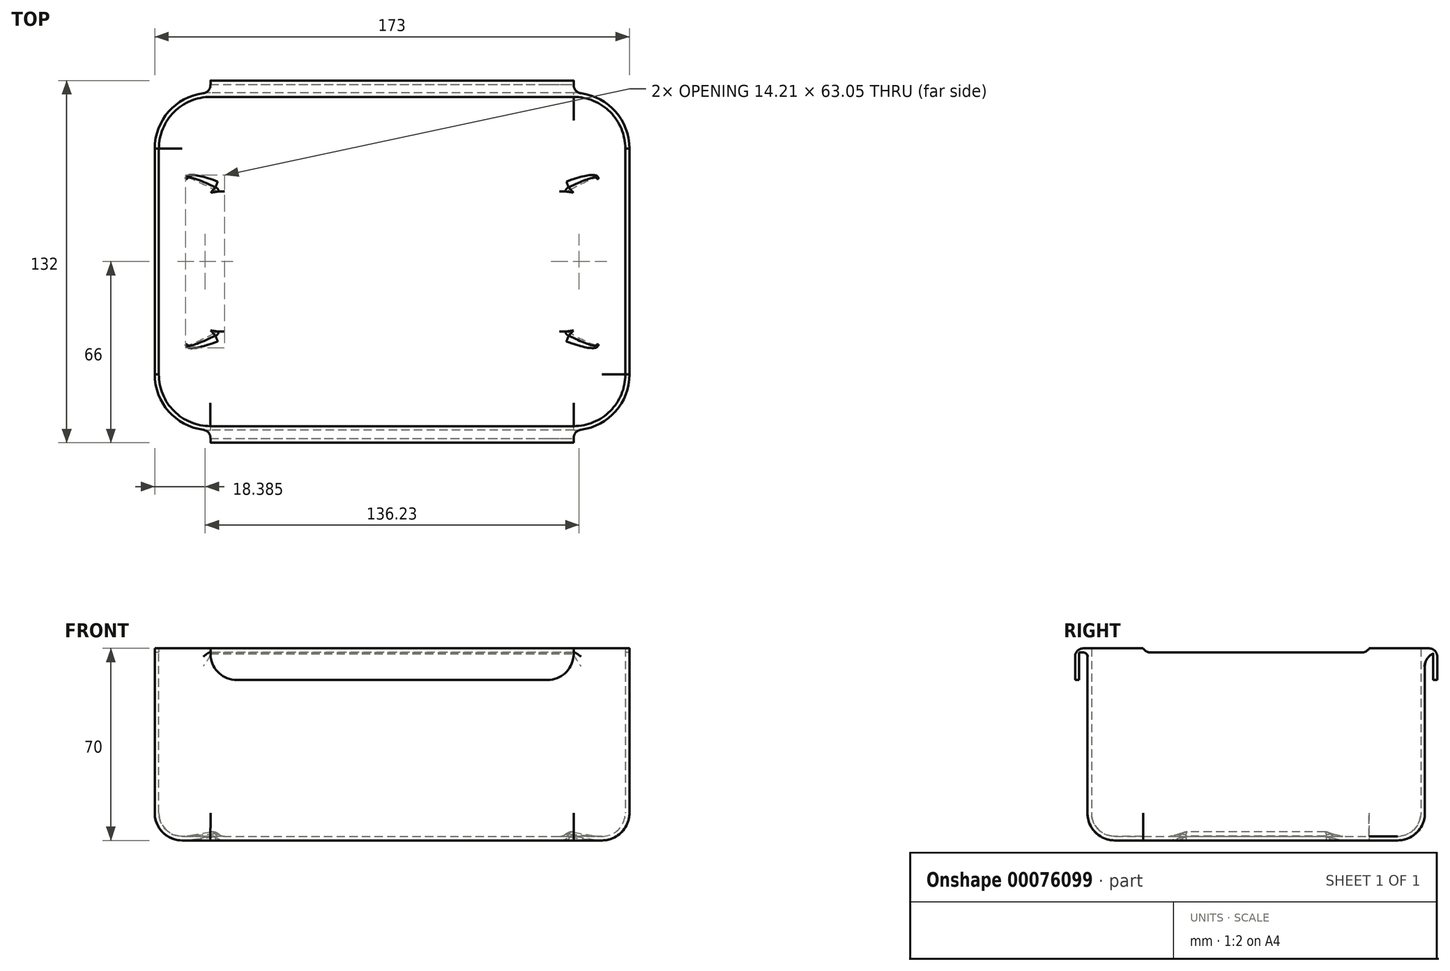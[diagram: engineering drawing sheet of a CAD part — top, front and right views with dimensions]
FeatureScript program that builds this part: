
annotation { "Feature Type Name" : "Feature", "Feature Type Description" : "" }
export const myFeature = defineFeature(function(context is Context, id is Id, definition is map)
    precondition{}
    {
        {
            var Q0;
            Q0=qCreatedBy(makeId("Top.planeOp"),FACE);
            var sketch = newSketch(context, id + "F0", { "sketchPlane" : qUnion([Q0])});
            skLineSegment(sketch, "E0.bottom", {"start": v(66.18, -61.5) * mm, "end": v(-66.18, -61.5) * mm});
            skLineSegment(sketch, "E0.top", {"start": v(66.18, 61.5) * mm, "end": v(-66.18, 61.5) * mm});
            skLineSegment(sketch, "E0.left", {"start": v(86.5, -41.18) * mm, "end": v(86.5, 41.18) * mm});
            skLineSegment(sketch, "E0.right", {"start": v(-86.5, -41.18) * mm, "end": v(-86.5, 41.18) * mm});
            skPoint(sketch, "E0.middle", {"position": v(0, 0) * mm});
            skPoint(sketch, "E1.visualSharp", {"position": v(-86.5, 61.5) * mm});
            skArc(sketch, "E1.filletArc", {"start": v(-66.18, 61.5) * mm, "mid": v(-80.55, 55.55) * mm, "end": v(-86.5, 41.18) * mm});
            skPoint(sketch, "E2.visualSharp", {"position": v(86.5, 61.5) * mm});
            skArc(sketch, "E2.filletArc", {"start": v(86.5, 41.18) * mm, "mid": v(80.55, 55.55) * mm, "end": v(66.18, 61.5) * mm});
            skPoint(sketch, "E3.visualSharp", {"position": v(86.5, -61.5) * mm});
            skArc(sketch, "E3.filletArc", {"start": v(66.18, -61.5) * mm, "mid": v(80.55, -55.55) * mm, "end": v(86.5, -41.18) * mm});
            skPoint(sketch, "E4.visualSharp", {"position": v(-86.5, -61.5) * mm});
            skArc(sketch, "E4.filletArc", {"start": v(-86.5, -41.18) * mm, "mid": v(-80.55, -55.55) * mm, "end": v(-66.18, -61.5) * mm});
            skSolve(sketch);
        }
        {
            var Q0;
            Q0=makeQuery(id+"F0.imprint","IMPRINT",FACE,{"disambiguationData":[TD([[makeQuery(id+"F0.imprint","IMPRINT",EDGE,{"derivedFrom":sQuery(id+"F0.wireOp",EDGE,"E0.bottom")}),-1.0]])]});
            extrude(context, id + "F1", {"entities" : qUnion([Q0]), "depth" : 70 * mm});
        }
        {
            var Q0;
            Q0=makeQuery(id+"F1.opExtrude","CAP_FACE",FACE,{"disambiguationData":[OSD([sQuery(id+"F0.wireOp",EDGE,"E0.bottom"),sQuery(id+"F0.wireOp",EDGE,"E0.top"),sQuery(id+"F0.wireOp",EDGE,"E0.left"),sQuery(id+"F0.wireOp",EDGE,"E0.right"),sQuery(id+"F0.wireOp",EDGE,"E1.filletArc"),sQuery(id+"F0.wireOp",EDGE,"E2.filletArc"),sQuery(id+"F0.wireOp",EDGE,"E3.filletArc"),sQuery(id+"F0.wireOp",EDGE,"E4.filletArc")])],"isStart":true});
            fillet(context, id + "F2", {"entities" : qUnion([Q0]), "radius" : 10 * mm, "tangentPropagation" : true, "allowEdgeOverflow" : false});
        }
        {
            var Q0;
            Q0=makeQuery(id+"F1.opExtrude","CAP_FACE",FACE,{"disambiguationData":[OSD([sQuery(id+"F0.wireOp",EDGE,"E0.bottom"),sQuery(id+"F0.wireOp",EDGE,"E0.top"),sQuery(id+"F0.wireOp",EDGE,"E0.left"),sQuery(id+"F0.wireOp",EDGE,"E0.right"),sQuery(id+"F0.wireOp",EDGE,"E1.filletArc"),sQuery(id+"F0.wireOp",EDGE,"E2.filletArc"),sQuery(id+"F0.wireOp",EDGE,"E3.filletArc"),sQuery(id+"F0.wireOp",EDGE,"E4.filletArc")])],"isStart":true});
            var sketch = newSketch(context, id + "F3", { "sketchPlane" : qUnion([Q0])});
            skLineSegment(sketch, "E5", {"start": v(74.78, 0) * mm, "end": v(74.78, 32.96) * mm});
            skLineSegment(sketch, "E6", {"start": v(74.78, 32.96) * mm, "end": v(62.04, 25.39) * mm});
            skLineSegment(sketch, "E7", {"start": v(62.04, 25.39) * mm, "end": v(62.04, 0) * mm});
            skLineSegment(sketch, "E8.MirrorCS", {"start": v(62.04, -25.39) * mm, "end": v(62.04, 0) * mm});
            skLineSegment(sketch, "E9.MirrorCS", {"start": v(74.78, 0) * mm, "end": v(74.78, -32.96) * mm});
            skLineSegment(sketch, "E10.MirrorCS", {"start": v(74.78, -32.96) * mm, "end": v(62.04, -25.39) * mm});
            skLineSegment(sketch, "E11.MirrorCS", {"start": v(-74.78, 0) * mm, "end": v(-74.78, -32.96) * mm});
            skLineSegment(sketch, "E12.MirrorCS", {"start": v(-74.78, -32.96) * mm, "end": v(-62.04, -25.39) * mm});
            skLineSegment(sketch, "E13.MirrorCS", {"start": v(-62.04, -25.39) * mm, "end": v(-62.04, 0) * mm});
            skLineSegment(sketch, "E14.MirrorCS", {"start": v(-62.04, 25.39) * mm, "end": v(-62.04, 0) * mm});
            skLineSegment(sketch, "E15.MirrorCS", {"start": v(-74.78, 0) * mm, "end": v(-74.78, 32.96) * mm});
            skLineSegment(sketch, "E16.MirrorCS", {"start": v(-74.78, 32.96) * mm, "end": v(-62.04, 25.39) * mm});
            skSolve(sketch);
        }
        {
            var Q0;
            Q0 = qSketchRegion(id + "F3", true);
            extrude(context, id + "F4", {"entities" : qUnion([Q0]), "operationType" : NewBodyOperationType.REMOVE, "oppositeDirection" : true, "depth" : 2 * mm});
        }
        {
            var Q0;
            Q0=makeQuery(id+"F4.boolean.opBoolean","COPY",EDGE,{"derivedFrom":makeQuery(id+"F4.opExtrude","CAP_EDGE",EDGE,{"disambiguationData":[OSD([sQuery(id+"F3.wireOp",EDGE,"E11.MirrorCS"),sQuery(id+"F3.wireOp",EDGE,"E15.MirrorCS")])],"isStart":false})});
            var Q1;
            Q1=makeQuery(id+"F4.boolean.opBoolean","COPY",EDGE,{"derivedFrom":makeQuery(id+"F4.opExtrude","CAP_EDGE",EDGE,{"disambiguationData":[OSD([sQuery(id+"F3.wireOp",EDGE,"E5"),sQuery(id+"F3.wireOp",EDGE,"E9.MirrorCS")])],"isStart":false})});
            chamfer(context, id + "F5", {"entities" : qUnion([Q0, Q1]), "chamferType" : ChamferType.OFFSET_ANGLE, "width" : 2 * mm, "oppositeDirection" : false, "angle" : 80 * degree, "tangentPropagation" : true});
        }
        {
            var Q0;
            Q0=makeQuery(id+"F4.boolean.opBoolean","COPY",EDGE,{"derivedFrom":makeQuery(id+"F4.opExtrude","CAP_EDGE",EDGE,{"disambiguationData":[OSD([sQuery(id+"F3.wireOp",EDGE,"E13.MirrorCS"),sQuery(id+"F3.wireOp",EDGE,"E14.MirrorCS")])],"isStart":false})});
            var Q1;
            Q1=makeQuery(id+"F4.boolean.opBoolean","COPY",EDGE,{"derivedFrom":makeQuery(id+"F4.opExtrude","CAP_EDGE",EDGE,{"disambiguationData":[OSD([sQuery(id+"F3.wireOp",EDGE,"E7"),sQuery(id+"F3.wireOp",EDGE,"E8.MirrorCS")])],"isStart":false})});
            chamfer(context, id + "F6", {"entities" : qUnion([Q0, Q1]), "width" : 3 * mm, "tangentPropagation" : true});
        }
        {
            var Q0;
            Q0=makeQuery(id+"F5.opChamfer","BLEND_EDGE",EDGE,{"blendedFrom":[makeQuery(id+"F4.boolean.opBoolean","COPY",EDGE,{"derivedFrom":makeQuery(id+"F4.opExtrude","CAP_EDGE",EDGE,{"disambiguationData":[OSD([sQuery(id+"F3.wireOp",EDGE,"E5"),sQuery(id+"F3.wireOp",EDGE,"E9.MirrorCS")])],"isStart":false})}),makeQuery(id+"F4.boolean.opBoolean","COPY",FACE,{"derivedFrom":makeQuery(id+"F4.opExtrude","SWEPT_FACE",FACE,{"disambiguationData":[OSD([sQuery(id+"F3.wireOp",EDGE,"E10.MirrorCS")])]})})],"blendedInto":[makeQuery(id+"F4.boolean.opBoolean","COPY",FACE,{"derivedFrom":makeQuery(id+"F4.opExtrude","SWEPT_FACE",FACE,{"disambiguationData":[OSD([sQuery(id+"F3.wireOp",EDGE,"E10.MirrorCS")])]})})]});
            var Q1;
            Q1=makeQuery(id+"F6.opChamfer","BLEND_EDGE",EDGE,{"blendedFrom":[makeQuery(id+"F4.boolean.opBoolean","COPY",EDGE,{"derivedFrom":makeQuery(id+"F4.opExtrude","CAP_EDGE",EDGE,{"disambiguationData":[OSD([sQuery(id+"F3.wireOp",EDGE,"E7"),sQuery(id+"F3.wireOp",EDGE,"E8.MirrorCS")])],"isStart":false})}),makeQuery(id+"F5.opChamfer","BLEND_FACE",FACE,{"disambiguationData":[OSD([sQuery(id+"F3.wireOp",EDGE,"E5"),sQuery(id+"F3.wireOp",EDGE,"E9.MirrorCS")])]})],"blendedInto":[makeQuery(id+"F5.opChamfer","BLEND_FACE",FACE,{"disambiguationData":[OSD([sQuery(id+"F3.wireOp",EDGE,"E5"),sQuery(id+"F3.wireOp",EDGE,"E9.MirrorCS")])]})]});
            var Q2;
            Q2=makeQuery(id+"F5.opChamfer","BLEND_EDGE",EDGE,{"blendedFrom":[makeQuery(id+"F4.boolean.opBoolean","COPY",EDGE,{"derivedFrom":makeQuery(id+"F4.opExtrude","CAP_EDGE",EDGE,{"disambiguationData":[OSD([sQuery(id+"F3.wireOp",EDGE,"E5"),sQuery(id+"F3.wireOp",EDGE,"E9.MirrorCS")])],"isStart":false})}),makeQuery(id+"F4.boolean.opBoolean","COPY",FACE,{"derivedFrom":makeQuery(id+"F4.opExtrude","SWEPT_FACE",FACE,{"disambiguationData":[OSD([sQuery(id+"F3.wireOp",EDGE,"E6")])]})})],"blendedInto":[makeQuery(id+"F4.boolean.opBoolean","COPY",FACE,{"derivedFrom":makeQuery(id+"F4.opExtrude","SWEPT_FACE",FACE,{"disambiguationData":[OSD([sQuery(id+"F3.wireOp",EDGE,"E6")])]})})]});
            var Q3;
            Q3=makeQuery(id+"F6.opChamfer","BLEND_EDGE",EDGE,{"blendedFrom":[makeQuery(id+"F4.boolean.opBoolean","COPY",EDGE,{"derivedFrom":makeQuery(id+"F4.opExtrude","CAP_EDGE",EDGE,{"disambiguationData":[OSD([sQuery(id+"F3.wireOp",EDGE,"E13.MirrorCS"),sQuery(id+"F3.wireOp",EDGE,"E14.MirrorCS")])],"isStart":false})}),makeQuery(id+"F5.opChamfer","BLEND_FACE",FACE,{"disambiguationData":[OSD([sQuery(id+"F3.wireOp",EDGE,"E11.MirrorCS"),sQuery(id+"F3.wireOp",EDGE,"E15.MirrorCS")])]})],"blendedInto":[makeQuery(id+"F5.opChamfer","BLEND_FACE",FACE,{"disambiguationData":[OSD([sQuery(id+"F3.wireOp",EDGE,"E11.MirrorCS"),sQuery(id+"F3.wireOp",EDGE,"E15.MirrorCS")])]})]});
            var Q4;
            Q4=makeQuery(id+"F5.opChamfer","BLEND_EDGE",EDGE,{"blendedFrom":[makeQuery(id+"F4.boolean.opBoolean","COPY",EDGE,{"derivedFrom":makeQuery(id+"F4.opExtrude","CAP_EDGE",EDGE,{"disambiguationData":[OSD([sQuery(id+"F3.wireOp",EDGE,"E11.MirrorCS"),sQuery(id+"F3.wireOp",EDGE,"E15.MirrorCS")])],"isStart":false})}),makeQuery(id+"F4.boolean.opBoolean","COPY",FACE,{"derivedFrom":makeQuery(id+"F4.opExtrude","SWEPT_FACE",FACE,{"disambiguationData":[OSD([sQuery(id+"F3.wireOp",EDGE,"E16.MirrorCS")])]})})],"blendedInto":[makeQuery(id+"F4.boolean.opBoolean","COPY",FACE,{"derivedFrom":makeQuery(id+"F4.opExtrude","SWEPT_FACE",FACE,{"disambiguationData":[OSD([sQuery(id+"F3.wireOp",EDGE,"E16.MirrorCS")])]})})]});
            var Q5;
            Q5=makeQuery(id+"F5.opChamfer","BLEND_EDGE",EDGE,{"blendedFrom":[makeQuery(id+"F4.boolean.opBoolean","COPY",EDGE,{"derivedFrom":makeQuery(id+"F4.opExtrude","CAP_EDGE",EDGE,{"disambiguationData":[OSD([sQuery(id+"F3.wireOp",EDGE,"E11.MirrorCS"),sQuery(id+"F3.wireOp",EDGE,"E15.MirrorCS")])],"isStart":false})}),makeQuery(id+"F4.boolean.opBoolean","COPY",FACE,{"derivedFrom":makeQuery(id+"F4.opExtrude","SWEPT_FACE",FACE,{"disambiguationData":[OSD([sQuery(id+"F3.wireOp",EDGE,"E12.MirrorCS")])]})})],"blendedInto":[makeQuery(id+"F4.boolean.opBoolean","COPY",FACE,{"derivedFrom":makeQuery(id+"F4.opExtrude","SWEPT_FACE",FACE,{"disambiguationData":[OSD([sQuery(id+"F3.wireOp",EDGE,"E12.MirrorCS")])]})})]});
            fillet(context, id + "F7", {"entities" : qUnion([Q0, Q1, Q2, Q3, Q4, Q5]), "radius" : 2 * mm, "tangentPropagation" : true, "allowEdgeOverflow" : false});
        }
        {
            var Q0;
            {var subQ0=sQuery(id+"F3.wireOp",EDGE,"E15.MirrorCS");var subQ1=sQuery(id+"F3.wireOp",EDGE,"E11.MirrorCS");Q0=makeQuery(id+"F7.opFillet","BLEND_EDGE",EDGE,{"blendedFrom":[makeQuery(id+"F6.opChamfer","BLEND_EDGE",EDGE,{"blendedFrom":[makeQuery(id+"F4.boolean.opBoolean","COPY",EDGE,{"derivedFrom":makeQuery(id+"F4.opExtrude","CAP_EDGE",EDGE,{"disambiguationData":[OSD([sQuery(id+"F3.wireOp",EDGE,"E13.MirrorCS"),sQuery(id+"F3.wireOp",EDGE,"E14.MirrorCS")])],"isStart":false})}),makeQuery(id+"F5.opChamfer","BLEND_FACE",FACE,{"disambiguationData":[OSD([subQ1,subQ0])]})],"blendedInto":[makeQuery(id+"F5.opChamfer","BLEND_FACE",FACE,{"disambiguationData":[OSD([subQ1,subQ0])]})]}),makeQuery(id+"F5.opChamfer","BLEND_EDGE",EDGE,{"blendedFrom":[makeQuery(id+"F4.boolean.opBoolean","COPY",EDGE,{"derivedFrom":makeQuery(id+"F4.opExtrude","CAP_EDGE",EDGE,{"disambiguationData":[OSD([subQ1,subQ0])],"isStart":false})}),makeQuery(id+"F4.boolean.opBoolean","COPY",FACE,{"derivedFrom":makeQuery(id+"F4.opExtrude","SWEPT_FACE",FACE,{"disambiguationData":[OSD([sQuery(id+"F3.wireOp",EDGE,"E16.MirrorCS")])]})})],"blendedInto":[makeQuery(id+"F4.boolean.opBoolean","COPY",FACE,{"derivedFrom":makeQuery(id+"F4.opExtrude","SWEPT_FACE",FACE,{"disambiguationData":[OSD([sQuery(id+"F3.wireOp",EDGE,"E16.MirrorCS")])]})})]})],"blendedInto":[]});}
            var Q1;
            Q1=makeQuery(id+"F7.opFillet","BLEND_EDGE",EDGE,{"blendedFrom":[makeQuery(id+"F5.opChamfer","BLEND_EDGE",EDGE,{"blendedFrom":[makeQuery(id+"F4.boolean.opBoolean","COPY",EDGE,{"derivedFrom":makeQuery(id+"F4.opExtrude","CAP_EDGE",EDGE,{"disambiguationData":[OSD([sQuery(id+"F3.wireOp",EDGE,"E11.MirrorCS"),sQuery(id+"F3.wireOp",EDGE,"E15.MirrorCS")])],"isStart":false})}),makeQuery(id+"F4.boolean.opBoolean","COPY",FACE,{"derivedFrom":makeQuery(id+"F4.opExtrude","SWEPT_FACE",FACE,{"disambiguationData":[OSD([sQuery(id+"F3.wireOp",EDGE,"E16.MirrorCS")])]})})],"blendedInto":[makeQuery(id+"F4.boolean.opBoolean","COPY",FACE,{"derivedFrom":makeQuery(id+"F4.opExtrude","SWEPT_FACE",FACE,{"disambiguationData":[OSD([sQuery(id+"F3.wireOp",EDGE,"E16.MirrorCS")])]})})]}),makeQuery(id+"F6.opChamfer","BLEND_FACE",FACE,{"disambiguationData":[OSD([sQuery(id+"F3.wireOp",EDGE,"E13.MirrorCS"),sQuery(id+"F3.wireOp",EDGE,"E14.MirrorCS")])]})],"blendedInto":[makeQuery(id+"F6.opChamfer","BLEND_FACE",FACE,{"disambiguationData":[OSD([sQuery(id+"F3.wireOp",EDGE,"E13.MirrorCS"),sQuery(id+"F3.wireOp",EDGE,"E14.MirrorCS")])]})]});
            var Q2;
            {var subQ0=sQuery(id+"F3.wireOp",EDGE,"E15.MirrorCS");var subQ1=sQuery(id+"F3.wireOp",EDGE,"E11.MirrorCS");Q2=makeQuery(id+"F7.opFillet","BLEND_EDGE",EDGE,{"blendedFrom":[makeQuery(id+"F6.opChamfer","BLEND_EDGE",EDGE,{"blendedFrom":[makeQuery(id+"F4.boolean.opBoolean","COPY",EDGE,{"derivedFrom":makeQuery(id+"F4.opExtrude","CAP_EDGE",EDGE,{"disambiguationData":[OSD([sQuery(id+"F3.wireOp",EDGE,"E13.MirrorCS"),sQuery(id+"F3.wireOp",EDGE,"E14.MirrorCS")])],"isStart":false})}),makeQuery(id+"F5.opChamfer","BLEND_FACE",FACE,{"disambiguationData":[OSD([subQ1,subQ0])]})],"blendedInto":[makeQuery(id+"F5.opChamfer","BLEND_FACE",FACE,{"disambiguationData":[OSD([subQ1,subQ0])]})]}),makeQuery(id+"F5.opChamfer","BLEND_EDGE",EDGE,{"blendedFrom":[makeQuery(id+"F4.boolean.opBoolean","COPY",EDGE,{"derivedFrom":makeQuery(id+"F4.opExtrude","CAP_EDGE",EDGE,{"disambiguationData":[OSD([subQ1,subQ0])],"isStart":false})}),makeQuery(id+"F4.boolean.opBoolean","COPY",FACE,{"derivedFrom":makeQuery(id+"F4.opExtrude","SWEPT_FACE",FACE,{"disambiguationData":[OSD([sQuery(id+"F3.wireOp",EDGE,"E12.MirrorCS")])]})})],"blendedInto":[makeQuery(id+"F4.boolean.opBoolean","COPY",FACE,{"derivedFrom":makeQuery(id+"F4.opExtrude","SWEPT_FACE",FACE,{"disambiguationData":[OSD([sQuery(id+"F3.wireOp",EDGE,"E12.MirrorCS")])]})})]})],"blendedInto":[]});}
            var Q3;
            {var subQ0=sQuery(id+"F3.wireOp",EDGE,"E9.MirrorCS");var subQ1=sQuery(id+"F3.wireOp",EDGE,"E5");Q3=makeQuery(id+"F7.opFillet","BLEND_EDGE",EDGE,{"blendedFrom":[makeQuery(id+"F6.opChamfer","BLEND_EDGE",EDGE,{"blendedFrom":[makeQuery(id+"F4.boolean.opBoolean","COPY",EDGE,{"derivedFrom":makeQuery(id+"F4.opExtrude","CAP_EDGE",EDGE,{"disambiguationData":[OSD([sQuery(id+"F3.wireOp",EDGE,"E7"),sQuery(id+"F3.wireOp",EDGE,"E8.MirrorCS")])],"isStart":false})}),makeQuery(id+"F5.opChamfer","BLEND_FACE",FACE,{"disambiguationData":[OSD([subQ1,subQ0])]})],"blendedInto":[makeQuery(id+"F5.opChamfer","BLEND_FACE",FACE,{"disambiguationData":[OSD([subQ1,subQ0])]})]}),makeQuery(id+"F5.opChamfer","BLEND_EDGE",EDGE,{"blendedFrom":[makeQuery(id+"F4.boolean.opBoolean","COPY",EDGE,{"derivedFrom":makeQuery(id+"F4.opExtrude","CAP_EDGE",EDGE,{"disambiguationData":[OSD([subQ1,subQ0])],"isStart":false})}),makeQuery(id+"F4.boolean.opBoolean","COPY",FACE,{"derivedFrom":makeQuery(id+"F4.opExtrude","SWEPT_FACE",FACE,{"disambiguationData":[OSD([sQuery(id+"F3.wireOp",EDGE,"E6")])]})})],"blendedInto":[makeQuery(id+"F4.boolean.opBoolean","COPY",FACE,{"derivedFrom":makeQuery(id+"F4.opExtrude","SWEPT_FACE",FACE,{"disambiguationData":[OSD([sQuery(id+"F3.wireOp",EDGE,"E6")])]})})]})],"blendedInto":[]});}
            var Q4;
            {var subQ0=sQuery(id+"F3.wireOp",EDGE,"E9.MirrorCS");var subQ1=sQuery(id+"F3.wireOp",EDGE,"E5");Q4=makeQuery(id+"F7.opFillet","BLEND_EDGE",EDGE,{"blendedFrom":[makeQuery(id+"F6.opChamfer","BLEND_EDGE",EDGE,{"blendedFrom":[makeQuery(id+"F4.boolean.opBoolean","COPY",EDGE,{"derivedFrom":makeQuery(id+"F4.opExtrude","CAP_EDGE",EDGE,{"disambiguationData":[OSD([sQuery(id+"F3.wireOp",EDGE,"E7"),sQuery(id+"F3.wireOp",EDGE,"E8.MirrorCS")])],"isStart":false})}),makeQuery(id+"F5.opChamfer","BLEND_FACE",FACE,{"disambiguationData":[OSD([subQ1,subQ0])]})],"blendedInto":[makeQuery(id+"F5.opChamfer","BLEND_FACE",FACE,{"disambiguationData":[OSD([subQ1,subQ0])]})]}),makeQuery(id+"F5.opChamfer","BLEND_EDGE",EDGE,{"blendedFrom":[makeQuery(id+"F4.boolean.opBoolean","COPY",EDGE,{"derivedFrom":makeQuery(id+"F4.opExtrude","CAP_EDGE",EDGE,{"disambiguationData":[OSD([subQ1,subQ0])],"isStart":false})}),makeQuery(id+"F4.boolean.opBoolean","COPY",FACE,{"derivedFrom":makeQuery(id+"F4.opExtrude","SWEPT_FACE",FACE,{"disambiguationData":[OSD([sQuery(id+"F3.wireOp",EDGE,"E10.MirrorCS")])]})})],"blendedInto":[makeQuery(id+"F4.boolean.opBoolean","COPY",FACE,{"derivedFrom":makeQuery(id+"F4.opExtrude","SWEPT_FACE",FACE,{"disambiguationData":[OSD([sQuery(id+"F3.wireOp",EDGE,"E10.MirrorCS")])]})})]})],"blendedInto":[]});}
            fillet(context, id + "F8", {"entities" : qUnion([Q0, Q1, Q2, Q3, Q4]), "radius" : 1 * mm, "tangentPropagation" : true, "allowEdgeOverflow" : false});
        }
        {
            var Q0;
            Q0=makeQuery(id+"F6.opChamfer","BLEND_EDGE",EDGE,{"blendedFrom":[makeQuery(id+"F4.boolean.opBoolean","COPY",EDGE,{"derivedFrom":makeQuery(id+"F4.opExtrude","CAP_EDGE",EDGE,{"disambiguationData":[OSD([sQuery(id+"F3.wireOp",EDGE,"E7"),sQuery(id+"F3.wireOp",EDGE,"E8.MirrorCS")])],"isStart":false})}),makeQuery(id+"F1.opExtrude","CAP_FACE",FACE,{"disambiguationData":[OSD([sQuery(id+"F0.wireOp",EDGE,"E0.bottom"),sQuery(id+"F0.wireOp",EDGE,"E0.top"),sQuery(id+"F0.wireOp",EDGE,"E0.left"),sQuery(id+"F0.wireOp",EDGE,"E0.right"),sQuery(id+"F0.wireOp",EDGE,"E1.filletArc"),sQuery(id+"F0.wireOp",EDGE,"E2.filletArc"),sQuery(id+"F0.wireOp",EDGE,"E3.filletArc"),sQuery(id+"F0.wireOp",EDGE,"E4.filletArc")])],"isStart":true})],"blendedInto":[makeQuery(id+"F1.opExtrude","CAP_FACE",FACE,{"disambiguationData":[OSD([sQuery(id+"F0.wireOp",EDGE,"E0.bottom"),sQuery(id+"F0.wireOp",EDGE,"E0.top"),sQuery(id+"F0.wireOp",EDGE,"E0.left"),sQuery(id+"F0.wireOp",EDGE,"E0.right"),sQuery(id+"F0.wireOp",EDGE,"E1.filletArc"),sQuery(id+"F0.wireOp",EDGE,"E2.filletArc"),sQuery(id+"F0.wireOp",EDGE,"E3.filletArc"),sQuery(id+"F0.wireOp",EDGE,"E4.filletArc")])],"isStart":true})]});
            var Q1;
            Q1=makeQuery(id+"F6.opChamfer","BLEND_EDGE",EDGE,{"blendedFrom":[makeQuery(id+"F4.boolean.opBoolean","COPY",EDGE,{"derivedFrom":makeQuery(id+"F4.opExtrude","CAP_EDGE",EDGE,{"disambiguationData":[OSD([sQuery(id+"F3.wireOp",EDGE,"E13.MirrorCS"),sQuery(id+"F3.wireOp",EDGE,"E14.MirrorCS")])],"isStart":false})}),makeQuery(id+"F1.opExtrude","CAP_FACE",FACE,{"disambiguationData":[OSD([sQuery(id+"F0.wireOp",EDGE,"E0.bottom"),sQuery(id+"F0.wireOp",EDGE,"E0.top"),sQuery(id+"F0.wireOp",EDGE,"E0.left"),sQuery(id+"F0.wireOp",EDGE,"E0.right"),sQuery(id+"F0.wireOp",EDGE,"E1.filletArc"),sQuery(id+"F0.wireOp",EDGE,"E2.filletArc"),sQuery(id+"F0.wireOp",EDGE,"E3.filletArc"),sQuery(id+"F0.wireOp",EDGE,"E4.filletArc")])],"isStart":true})],"blendedInto":[makeQuery(id+"F1.opExtrude","CAP_FACE",FACE,{"disambiguationData":[OSD([sQuery(id+"F0.wireOp",EDGE,"E0.bottom"),sQuery(id+"F0.wireOp",EDGE,"E0.top"),sQuery(id+"F0.wireOp",EDGE,"E0.left"),sQuery(id+"F0.wireOp",EDGE,"E0.right"),sQuery(id+"F0.wireOp",EDGE,"E1.filletArc"),sQuery(id+"F0.wireOp",EDGE,"E2.filletArc"),sQuery(id+"F0.wireOp",EDGE,"E3.filletArc"),sQuery(id+"F0.wireOp",EDGE,"E4.filletArc")])],"isStart":true})]});
            fillet(context, id + "F9", {"entities" : qUnion([Q0, Q1]), "radius" : 5 * mm, "tangentPropagation" : true, "allowEdgeOverflow" : false});
        }
        {
            var Q0;
            Q0=makeQuery(id+"F1.opExtrude","CAP_FACE",FACE,{"disambiguationData":[OSD([sQuery(id+"F0.wireOp",EDGE,"E0.bottom"),sQuery(id+"F0.wireOp",EDGE,"E0.top"),sQuery(id+"F0.wireOp",EDGE,"E0.left"),sQuery(id+"F0.wireOp",EDGE,"E0.right"),sQuery(id+"F0.wireOp",EDGE,"E1.filletArc"),sQuery(id+"F0.wireOp",EDGE,"E2.filletArc"),sQuery(id+"F0.wireOp",EDGE,"E3.filletArc"),sQuery(id+"F0.wireOp",EDGE,"E4.filletArc")])],"isStart":false});
            var sketch = newSketch(context, id + "F10", { "sketchPlane" : qUnion([Q0])});
            skLineSegment(sketch, "E17.top", {"start": v(-66.18, 66) * mm, "end": v(66.18, 66) * mm});
            skLineSegment(sketch, "E17.left", {"start": v(-66.18, 61.5) * mm, "end": v(-66.18, 66) * mm});
            skLineSegment(sketch, "E17.right", {"start": v(66.18, 61.5) * mm, "end": v(66.18, 66) * mm});
            skLineSegment(sketch, "E18.top", {"start": v(-66.18, -66) * mm, "end": v(66.18, -66) * mm});
            skLineSegment(sketch, "E18.left", {"start": v(-66.18, -61.5) * mm, "end": v(-66.18, -66) * mm});
            skLineSegment(sketch, "E18.right", {"start": v(66.18, -61.5) * mm, "end": v(66.18, -66) * mm});
            skArc(sketch, "E19.0", {"start": v(-66.18, 61.5) * mm, "mid": v(-80.55, 55.55) * mm, "end": v(-86.5, 41.18) * mm});
            skLineSegment(sketch, "E19.1", {"start": v(-86.5, -41.18) * mm, "end": v(-86.5, 41.18) * mm});
            skArc(sketch, "E19.2", {"start": v(-86.5, -41.18) * mm, "mid": v(-80.55, -55.55) * mm, "end": v(-66.18, -61.5) * mm});
            skArc(sketch, "E19.3", {"start": v(66.18, -61.5) * mm, "mid": v(80.55, -55.55) * mm, "end": v(86.5, -41.18) * mm});
            skLineSegment(sketch, "E19.4", {"start": v(86.5, -41.18) * mm, "end": v(86.5, 41.18) * mm});
            skArc(sketch, "E19.5", {"start": v(86.5, 41.18) * mm, "mid": v(80.55, 55.55) * mm, "end": v(66.18, 61.5) * mm});
            skSolve(sketch);
        }
        {
            var Q0;
            Q0 = qSketchRegion(id + "F10", true);
            extrude(context, id + "F11", {"entities" : qUnion([Q0]), "operationType" : NewBodyOperationType.ADD, "oppositeDirection" : true, "depth" : 1.5 * mm});
        }
        {
            var Q0;
            Q0=makeQuery(id+"F11.boolean.opBoolean","MERGE",FACE,{"derivedFrom":[makeQuery(id+"F1.opExtrude","CAP_FACE",FACE,{"disambiguationData":[OSD([sQuery(id+"F0.wireOp",EDGE,"E0.bottom"),sQuery(id+"F0.wireOp",EDGE,"E0.top"),sQuery(id+"F0.wireOp",EDGE,"E0.left"),sQuery(id+"F0.wireOp",EDGE,"E0.right"),sQuery(id+"F0.wireOp",EDGE,"E1.filletArc"),sQuery(id+"F0.wireOp",EDGE,"E2.filletArc"),sQuery(id+"F0.wireOp",EDGE,"E3.filletArc"),sQuery(id+"F0.wireOp",EDGE,"E4.filletArc")])],"isStart":false}),makeQuery(id+"F11.opExtrude","CAP_FACE",FACE,{"disambiguationData":[OSD([sQuery(id+"F10.wireOp",EDGE,"E17.top"),sQuery(id+"F10.wireOp",EDGE,"E17.left"),sQuery(id+"F10.wireOp",EDGE,"E17.right"),sQuery(id+"F10.wireOp",EDGE,"E18.top"),sQuery(id+"F10.wireOp",EDGE,"E18.left"),sQuery(id+"F10.wireOp",EDGE,"E18.right"),sQuery(id+"F10.wireOp",EDGE,"E19.0"),sQuery(id+"F10.wireOp",EDGE,"E19.1"),sQuery(id+"F10.wireOp",EDGE,"E19.2"),sQuery(id+"F10.wireOp",EDGE,"E19.3"),sQuery(id+"F10.wireOp",EDGE,"E19.4"),sQuery(id+"F10.wireOp",EDGE,"E19.5")])],"isStart":true})]});
            shell(context, id + "F12", {"entities" : qUnion([Q0]), "thickness" : 1.5 * mm});
        }
        {
            var Q0;
            {var subQ0=sQuery(id+"F10.wireOp",EDGE,"E17.top");var subQ1=sQuery(id+"F10.wireOp",EDGE,"E17.left");var subQ2=sQuery(id+"F10.wireOp",EDGE,"E17.right");Q0=makeQuery(id+"F11.boolean.opBoolean","SPLIT",FACE,{"disambiguationData":[TD([makeQuery(id+"F1.opExtrude","SWEPT_FACE",FACE,{"disambiguationData":[OSD([sQuery(id+"F0.wireOp",EDGE,"E0.top")])]})])],"derivedFrom":makeQuery(id+"F11.opExtrude","CAP_FACE",FACE,{"disambiguationData":[OSD([subQ0,subQ1,subQ2,sQuery(id+"F10.wireOp",EDGE,"E18.top"),sQuery(id+"F10.wireOp",EDGE,"E18.left"),sQuery(id+"F10.wireOp",EDGE,"E18.right"),sQuery(id+"F10.wireOp",EDGE,"E19.0"),sQuery(id+"F10.wireOp",EDGE,"E19.1"),sQuery(id+"F10.wireOp",EDGE,"E19.2"),sQuery(id+"F10.wireOp",EDGE,"E19.3"),sQuery(id+"F10.wireOp",EDGE,"E19.4"),sQuery(id+"F10.wireOp",EDGE,"E19.5")])],"isStart":false})});}
            var sketch = newSketch(context, id + "F13", { "sketchPlane" : qUnion([Q0])});
            skLineSegment(sketch, "E20.bottom", {"start": v(-66.18, -66) * mm, "end": v(66.18, -66) * mm});
            skLineSegment(sketch, "E20.top", {"start": v(-66.18, -64.5) * mm, "end": v(66.18, -64.5) * mm});
            skLineSegment(sketch, "E20.left", {"start": v(-66.18, -66) * mm, "end": v(-66.18, -64.5) * mm});
            skLineSegment(sketch, "E20.right", {"start": v(66.18, -66) * mm, "end": v(66.18, -64.5) * mm});
            skSolve(sketch);
        }
        {
            var Q0;
            Q0 = qSketchRegion(id + "F13", true);
            extrude(context, id + "F14", {"entities" : qUnion([Q0]), "operationType" : NewBodyOperationType.ADD, "depth" : 10 * mm});
        }
        {
            var Q0;
            {var subQ0=sQuery(id+"F10.wireOp",EDGE,"E18.top");var subQ1=sQuery(id+"F10.wireOp",EDGE,"E18.left");var subQ2=sQuery(id+"F10.wireOp",EDGE,"E18.right");Q0=makeQuery(id+"F11.boolean.opBoolean","SPLIT",FACE,{"disambiguationData":[TD([makeQuery(id+"F1.opExtrude","SWEPT_FACE",FACE,{"disambiguationData":[OSD([sQuery(id+"F0.wireOp",EDGE,"E0.bottom")])]})])],"derivedFrom":makeQuery(id+"F11.opExtrude","CAP_FACE",FACE,{"disambiguationData":[OSD([sQuery(id+"F10.wireOp",EDGE,"E17.top"),sQuery(id+"F10.wireOp",EDGE,"E17.left"),sQuery(id+"F10.wireOp",EDGE,"E17.right"),subQ0,subQ1,subQ2,sQuery(id+"F10.wireOp",EDGE,"E19.0"),sQuery(id+"F10.wireOp",EDGE,"E19.1"),sQuery(id+"F10.wireOp",EDGE,"E19.2"),sQuery(id+"F10.wireOp",EDGE,"E19.3"),sQuery(id+"F10.wireOp",EDGE,"E19.4"),sQuery(id+"F10.wireOp",EDGE,"E19.5")])],"isStart":false})});}
            var sketch = newSketch(context, id + "F15", { "sketchPlane" : qUnion([Q0])});
            skLineSegment(sketch, "E21.bottom", {"start": v(-66.18, 66) * mm, "end": v(66.18, 66) * mm});
            skLineSegment(sketch, "E21.top", {"start": v(-66.18, 64.5) * mm, "end": v(66.18, 64.5) * mm});
            skLineSegment(sketch, "E21.left", {"start": v(-66.18, 66) * mm, "end": v(-66.18, 64.5) * mm});
            skLineSegment(sketch, "E21.right", {"start": v(66.18, 66) * mm, "end": v(66.18, 64.5) * mm});
            skSolve(sketch);
        }
        {
            var Q0;
            Q0 = qSketchRegion(id + "F15", true);
            extrude(context, id + "F16", {"entities" : qUnion([Q0]), "operationType" : NewBodyOperationType.ADD, "depth" : 10 * mm});
        }
        {
            var Q0;
            {var subQ0=sQuery(id+"F0.wireOp",EDGE,"E0.bottom");Q0=makeQuery(id+"F11.boolean.opBoolean","MERGE",EDGE,{"derivedFrom":[makeQuery(id+"F1.opExtrude","SWEPT_EDGE",EDGE,{"disambiguationData":[OSD([subQ0,sQuery(id+"F0.wireOp",EDGE,"E4.filletArc")])]}),makeQuery(id+"F11.opExtrude","SWEPT_EDGE",EDGE,{"disambiguationData":[OSD([subQ0,sQuery(id+"F10.wireOp",EDGE,"E18.left"),sQuery(id+"F10.wireOp",EDGE,"E19.2")])]})]});}
            var Q1;
            {var subQ0=sQuery(id+"F0.wireOp",EDGE,"E0.bottom");Q1=makeQuery(id+"F11.boolean.opBoolean","MERGE",EDGE,{"derivedFrom":[makeQuery(id+"F1.opExtrude","SWEPT_EDGE",EDGE,{"disambiguationData":[OSD([subQ0,sQuery(id+"F0.wireOp",EDGE,"E3.filletArc")])]}),makeQuery(id+"F11.opExtrude","SWEPT_EDGE",EDGE,{"disambiguationData":[OSD([subQ0,sQuery(id+"F10.wireOp",EDGE,"E18.right"),sQuery(id+"F10.wireOp",EDGE,"E19.3")])]})]});}
            var Q2;
            {var subQ0=sQuery(id+"F0.wireOp",EDGE,"E0.top");Q2=makeQuery(id+"F11.boolean.opBoolean","MERGE",EDGE,{"derivedFrom":[makeQuery(id+"F1.opExtrude","SWEPT_EDGE",EDGE,{"disambiguationData":[OSD([subQ0,sQuery(id+"F0.wireOp",EDGE,"E2.filletArc")])]}),makeQuery(id+"F11.opExtrude","SWEPT_EDGE",EDGE,{"disambiguationData":[OSD([subQ0,sQuery(id+"F10.wireOp",EDGE,"E17.right"),sQuery(id+"F10.wireOp",EDGE,"E19.5")])]})]});}
            var Q3;
            {var subQ0=sQuery(id+"F0.wireOp",EDGE,"E0.top");Q3=makeQuery(id+"F11.boolean.opBoolean","MERGE",EDGE,{"derivedFrom":[makeQuery(id+"F1.opExtrude","SWEPT_EDGE",EDGE,{"disambiguationData":[OSD([subQ0,sQuery(id+"F0.wireOp",EDGE,"E1.filletArc")])]}),makeQuery(id+"F11.opExtrude","SWEPT_EDGE",EDGE,{"disambiguationData":[OSD([subQ0,sQuery(id+"F10.wireOp",EDGE,"E17.left"),sQuery(id+"F10.wireOp",EDGE,"E19.0")])]})]});}
            fillet(context, id + "F17", {"entities" : qUnion([Q0, Q1, Q2, Q3]), "radius" : 3.03 * mm, "tangentPropagation" : true, "allowEdgeOverflow" : false});
        }
        {
            var Q0;
            Q0=makeQuery(id+"F11.boolean.opBoolean","INTERSECT",EDGE,{"derivedFrom":[makeQuery(id+"F1.opExtrude","SWEPT_FACE",FACE,{"disambiguationData":[OSD([sQuery(id+"F0.wireOp",EDGE,"E0.top")])]}),makeQuery(id+"F11.opExtrude","CAP_FACE",FACE,{"disambiguationData":[OSD([sQuery(id+"F10.wireOp",EDGE,"E17.top"),sQuery(id+"F10.wireOp",EDGE,"E17.left"),sQuery(id+"F10.wireOp",EDGE,"E17.right"),sQuery(id+"F10.wireOp",EDGE,"E18.top"),sQuery(id+"F10.wireOp",EDGE,"E18.left"),sQuery(id+"F10.wireOp",EDGE,"E18.right"),sQuery(id+"F10.wireOp",EDGE,"E19.0"),sQuery(id+"F10.wireOp",EDGE,"E19.1"),sQuery(id+"F10.wireOp",EDGE,"E19.2"),sQuery(id+"F10.wireOp",EDGE,"E19.3"),sQuery(id+"F10.wireOp",EDGE,"E19.4"),sQuery(id+"F10.wireOp",EDGE,"E19.5")])],"isStart":false})]});
            fillet(context, id + "F18", {"entities" : qUnion([Q0]), "radius" : 5 * mm, "tangentPropagation" : true, "allowEdgeOverflow" : false});
        }
        {
            var Q0;
            Q0=makeQuery(id+"F11.boolean.opBoolean","INTERSECT",EDGE,{"derivedFrom":[makeQuery(id+"F1.opExtrude","SWEPT_FACE",FACE,{"disambiguationData":[OSD([sQuery(id+"F0.wireOp",EDGE,"E0.top")])]}),makeQuery(id+"F11.opExtrude","CAP_FACE",FACE,{"disambiguationData":[OSD([sQuery(id+"F10.wireOp",EDGE,"E17.top"),sQuery(id+"F10.wireOp",EDGE,"E17.left"),sQuery(id+"F10.wireOp",EDGE,"E17.right"),sQuery(id+"F10.wireOp",EDGE,"E18.top"),sQuery(id+"F10.wireOp",EDGE,"E18.left"),sQuery(id+"F10.wireOp",EDGE,"E18.right"),sQuery(id+"F10.wireOp",EDGE,"E19.0"),sQuery(id+"F10.wireOp",EDGE,"E19.1"),sQuery(id+"F10.wireOp",EDGE,"E19.2"),sQuery(id+"F10.wireOp",EDGE,"E19.3"),sQuery(id+"F10.wireOp",EDGE,"E19.4"),sQuery(id+"F10.wireOp",EDGE,"E19.5")])],"isStart":false})]});
            var Q1;
            Q1=makeQuery(id+"F14.opExtrude","CAP_EDGE",EDGE,{"disambiguationData":[OSD([sQuery(id+"F13.wireOp",EDGE,"E20.top")])],"isStart":true});
            var Q2;
            Q2=makeQuery(id+"F11.boolean.opBoolean","INTERSECT",EDGE,{"derivedFrom":[makeQuery(id+"F1.opExtrude","SWEPT_FACE",FACE,{"disambiguationData":[OSD([sQuery(id+"F0.wireOp",EDGE,"E0.bottom")])]}),makeQuery(id+"F11.opExtrude","CAP_FACE",FACE,{"disambiguationData":[OSD([sQuery(id+"F10.wireOp",EDGE,"E17.top"),sQuery(id+"F10.wireOp",EDGE,"E17.left"),sQuery(id+"F10.wireOp",EDGE,"E17.right"),sQuery(id+"F10.wireOp",EDGE,"E18.top"),sQuery(id+"F10.wireOp",EDGE,"E18.left"),sQuery(id+"F10.wireOp",EDGE,"E18.right"),sQuery(id+"F10.wireOp",EDGE,"E19.0"),sQuery(id+"F10.wireOp",EDGE,"E19.1"),sQuery(id+"F10.wireOp",EDGE,"E19.2"),sQuery(id+"F10.wireOp",EDGE,"E19.3"),sQuery(id+"F10.wireOp",EDGE,"E19.4"),sQuery(id+"F10.wireOp",EDGE,"E19.5")])],"isStart":false})]});
            var Q3;
            Q3=makeQuery(id+"F16.opExtrude","CAP_EDGE",EDGE,{"disambiguationData":[OSD([sQuery(id+"F15.wireOp",EDGE,"E21.top")])],"isStart":true});
            fillet(context, id + "F19", {"entities" : qUnion([Q0, Q1, Q2, Q3]), "radius" : 1.5 * mm, "tangentPropagation" : true, "allowEdgeOverflow" : false});
        }
        {
            var Q0;
            Q0=makeQuery(id+"F11.opExtrude","CAP_EDGE",EDGE,{"disambiguationData":[OSD([sQuery(id+"F10.wireOp",EDGE,"E18.top")])],"isStart":true});
            var Q1;
            Q1=makeQuery(id+"F11.opExtrude","CAP_EDGE",EDGE,{"disambiguationData":[OSD([sQuery(id+"F10.wireOp",EDGE,"E17.top")])],"isStart":true});
            fillet(context, id + "F20", {"entities" : qUnion([Q0, Q1]), "radius" : 3 * mm, "tangentPropagation" : true, "allowEdgeOverflow" : false});
        }
        {
            var Q0;
            Q0=makeQuery(id+"F14.opExtrude","CAP_EDGE",EDGE,{"disambiguationData":[OSD([sQuery(id+"F13.wireOp",EDGE,"E20.left")])],"isStart":false});
            var Q1;
            Q1=makeQuery(id+"F14.opExtrude","CAP_EDGE",EDGE,{"disambiguationData":[OSD([sQuery(id+"F13.wireOp",EDGE,"E20.right")])],"isStart":false});
            var Q2;
            Q2=makeQuery(id+"F16.opExtrude","CAP_EDGE",EDGE,{"disambiguationData":[OSD([sQuery(id+"F15.wireOp",EDGE,"E21.right")])],"isStart":false});
            var Q3;
            Q3=makeQuery(id+"F16.opExtrude","CAP_EDGE",EDGE,{"disambiguationData":[OSD([sQuery(id+"F15.wireOp",EDGE,"E21.left")])],"isStart":false});
            fillet(context, id + "F21", {"entities" : qUnion([Q0, Q1, Q2, Q3]), "radius" : 9.54 * mm, "tangentPropagation" : true, "allowEdgeOverflow" : false});
        }
        {
            var Q0;
            Q0=makeQuery(id+"F1.opExtrude","SWEPT_FACE",FACE,{"disambiguationData":[OSD([sQuery(id+"F0.wireOp",EDGE,"E0.left")])]});
            var sketch = newSketch(context, id + "F22", { "sketchPlane" : qUnion([Q0])});
            skLineSegment(sketch, "E22.0", {"start": v(-41.18, 68.5) * mm, "end": v(41.18, 68.5) * mm});
            skLineSegment(sketch, "E23", {"start": v(-41.18, 68.5) * mm, "end": v(-41.18, 70) * mm});
            skLineSegment(sketch, "E24", {"start": v(-41.18, 70) * mm, "end": v(41.18, 70) * mm});
            skLineSegment(sketch, "E25", {"start": v(41.18, 70) * mm, "end": v(41.18, 68.5) * mm});
            skSolve(sketch);
        }
        {
            var Q0;
            Q0 = qSketchRegion(id + "F22", true);
            extrude(context, id + "F23", {"entities" : qUnion([Q0]), "operationType" : NewBodyOperationType.REMOVE, "oppositeDirection" : true, "depth" : 182.2 * mm});
        }
        {
            var Q0;
            Q0=makeQuery(id+"F23.boolean.opBoolean","COPY",EDGE,{"disambiguationData":[OD(1.0)],"derivedFrom":makeQuery(id+"F23.opExtrude","SWEPT_EDGE",EDGE,{"disambiguationData":[OSD([sQuery(id+"F0.wireOp",EDGE,"E0.left"),sQuery(id+"F0.wireOp",EDGE,"E3.filletArc"),sQuery(id+"F22.wireOp",EDGE,"E22.0"),sQuery(id+"F22.wireOp",EDGE,"E23")])]})});
            var Q1;
            Q1=makeQuery(id+"F23.boolean.opBoolean","COPY",EDGE,{"disambiguationData":[OD(1.0)],"derivedFrom":makeQuery(id+"F23.opExtrude","SWEPT_EDGE",EDGE,{"disambiguationData":[OSD([sQuery(id+"F0.wireOp",EDGE,"E0.left"),sQuery(id+"F0.wireOp",EDGE,"E2.filletArc"),sQuery(id+"F22.wireOp",EDGE,"E22.0"),sQuery(id+"F22.wireOp",EDGE,"E25")])]})});
            var Q2;
            Q2=makeQuery(id+"F23.boolean.opBoolean","COPY",EDGE,{"disambiguationData":[OD(0.0)],"derivedFrom":makeQuery(id+"F23.opExtrude","SWEPT_EDGE",EDGE,{"disambiguationData":[OSD([sQuery(id+"F0.wireOp",EDGE,"E0.left"),sQuery(id+"F0.wireOp",EDGE,"E2.filletArc"),sQuery(id+"F22.wireOp",EDGE,"E22.0"),sQuery(id+"F22.wireOp",EDGE,"E25")])]})});
            var Q3;
            Q3=makeQuery(id+"F23.boolean.opBoolean","COPY",EDGE,{"disambiguationData":[OD(0.0)],"derivedFrom":makeQuery(id+"F23.opExtrude","SWEPT_EDGE",EDGE,{"disambiguationData":[OSD([sQuery(id+"F0.wireOp",EDGE,"E0.left"),sQuery(id+"F0.wireOp",EDGE,"E3.filletArc"),sQuery(id+"F22.wireOp",EDGE,"E22.0"),sQuery(id+"F22.wireOp",EDGE,"E23")])]})});
            fillet(context, id + "F24", {"entities" : qUnion([Q0, Q1, Q2, Q3]), "radius" : 3 * mm, "tangentPropagation" : true, "allowEdgeOverflow" : false});
        }
    });
